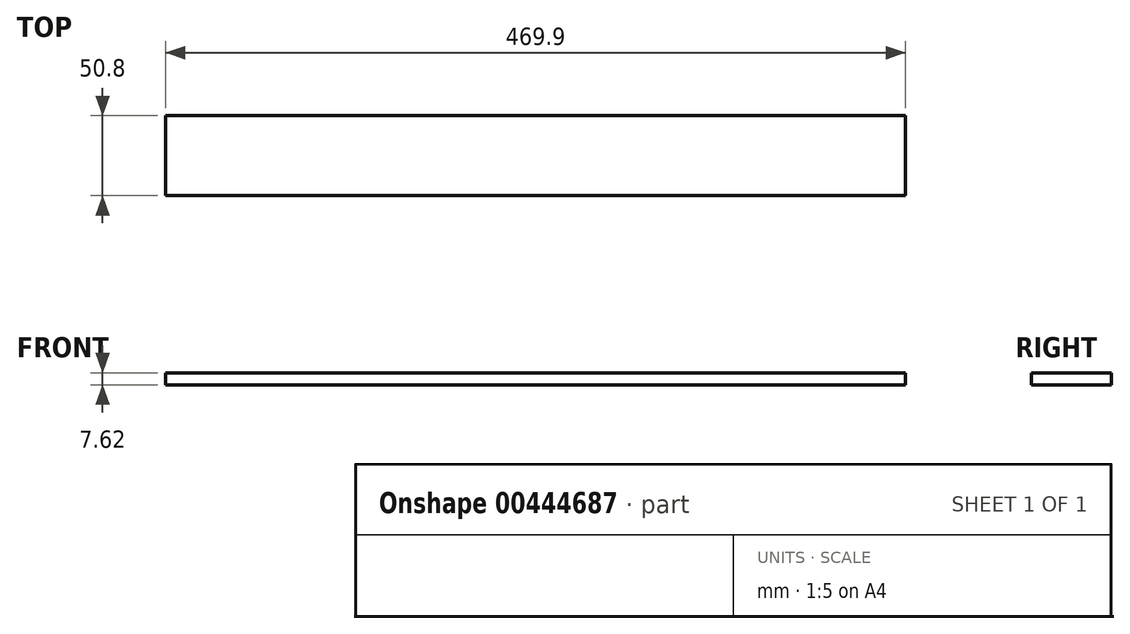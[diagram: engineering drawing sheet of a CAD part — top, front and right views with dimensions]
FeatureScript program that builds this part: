
annotation { "Feature Type Name" : "Feature", "Feature Type Description" : "" }
export const myFeature = defineFeature(function(context is Context, id is Id, definition is map)
    precondition{}
    {
        {
            var Q0;
            Q0=qCreatedBy(makeId("Top.planeOp"),FACE);
            var sketch = newSketch(context, id + "F0", { "sketchPlane" : qUnion([Q0])});
            skLineSegment(sketch, "E0.bottom", {"start": v(-229.25, 40.41) * mm, "end": v(240.65, 40.41) * mm});
            skLineSegment(sketch, "E0.top", {"start": v(-229.25, -10.39) * mm, "end": v(240.65, -10.39) * mm});
            skLineSegment(sketch, "E0.left", {"start": v(-229.25, 40.41) * mm, "end": v(-229.25, -10.39) * mm});
            skLineSegment(sketch, "E0.right", {"start": v(240.65, 40.41) * mm, "end": v(240.65, -10.39) * mm});
            skSolve(sketch);
        }
        {
            var Q0;
            Q0 = qSketchRegion(id + "F0", true);
            extrude(context, id + "F1", {"entities" : qUnion([Q0]), "depth" : 7.62 * mm});
        }
    });
